# Revit family: AISC ST Shapes-Top
name_source: partatom
category: Detail Items
revit_build: Autodesk Revit Architecture 2012 (Build: 20110210_1515)
units: mm (PartAtom-declared; Revit-internal decimal feet)

## types (28) — shared parameters
Keynote = 05 12 00.J0
y = 0' - 2 15/16"

## per-type parameters (varying)
| type | A | W | bf | d | k | tf | tw |
| ST12X60.5 | 0.12 SF | 60.5 | 0' - 8 1/16" | 1' - 0 5/16" | 0' - 2" | 0' - 1 3/32" | 0' - 0 13/16" |
| ST12X53 | 0.11 SF | 53 | 0' - 7 7/8" | 1' - 0 5/16" | 0' - 2" | 0' - 1 3/32" | 0' - 0 5/8" |
| ST12X50 | 0.1 SF | 50 | 0' - 7 1/4" | 1' - 0" | 0' - 1 3/4" | 0' - 0 7/8" | 0' - 0 3/4" |
| ST12X45 | 0.09 SF | 45 | 0' - 7 1/8" | 1' - 0" | 0' - 1 3/4" | 0' - 0 7/8" | 0' - 0 5/8" |
| ST12X40 | 0.08 SF | 40 | 0' - 7" | 1' - 0" | 0' - 1 3/4" | 0' - 0 7/8" | 0' - 0 1/2" |
| ST10X48 | 0.1 SF | 48 | 0' - 7 3/16" | 0' - 10 3/16" | 0' - 1 3/4" | 0' - 0 29/32" | 0' - 0 13/16" |
| ST10X43 | 0.09 SF | 43 | 0' - 7 1/16" | 0' - 10 3/16" | 0' - 1 3/4" | 0' - 0 29/32" | 0' - 0 21/32" |
| ST10X37.5 | 0.08 SF | 37.5 | 0' - 6 3/8" | 0' - 10" | 0' - 1 5/8" | 0' - 0 25/32" | 0' - 0 5/8" |
| ST10X33 | 0.07 SF | 33 | 0' - 6 1/4" | 0' - 10" | 0' - 1 5/8" | 0' - 0 25/32" | 0' - 0 1/2" |
| ST9X35 | 0.07 SF | 35 | 0' - 6 1/4" | 0' - 9" | 0' - 1 1/2" | 0' - 0 11/16" | 0' - 0 23/32" |
| ST9X27.35 | 0.06 SF | 27.4 | 0' - 6" | 0' - 9" | 0' - 1 1/2" | 0' - 0 11/16" | 0' - 0 15/32" |
| ST7.5X25 | 0.05 SF | 25 | 0' - 5 5/8" | 0' - 7 1/2" | 0' - 1 3/8" | 0' - 0 5/8" | 0' - 0 9/16" |
| ST7.5X21.45 | 0.04 SF | 21.5 | 0' - 5 1/2" | 0' - 7 1/2" | 0' - 1 3/8" | 0' - 0 5/8" | 0' - 0 13/32" |
| ST6X25 | 0.05 SF | 25 | 0' - 5 15/32" | 0' - 6" | 0' - 1 7/16" | 0' - 0 21/32" | 0' - 0 11/16" |
| ST6X20.4 | 0.04 SF | 20.4 | 0' - 5 1/4" | 0' - 6" | 0' - 1 7/16" | 0' - 0 21/32" | 0' - 0 15/32" |
| ST6X17.5 | 0.04 SF | 17.5 | 0' - 5 3/32" | 0' - 6" | 0' - 1 3/16" | 0' - 0 17/32" | 0' - 0 7/16" |
| ST6X15.9 | 0.03 SF | 15.9 | 0' - 5" | 0' - 6" | 0' - 1 3/16" | 0' - 0 17/32" | 0' - 0 11/32" |
| ST5X17.5 | 0.04 SF | 17.5 | 0' - 4 15/16" | 0' - 5" | 0' - 1 1/8" | 0' - 0 1/2" | 0' - 0 19/32" |
| ST5X12.7 | 0.03 SF | 12.7 | 0' - 4 21/32" | 0' - 5" | 0' - 1 1/8" | 0' - 0 1/2" | 0' - 0 5/16" |
| ST4X11.5 | 0.02 SF | 11.5 | 0' - 4 5/32" | 0' - 4" | 0' - 1" | 0' - 0 7/16" | 0' - 0 7/16" |
| ST4X9.2 | 0.02 SF | 9.2 | 0' - 4" | 0' - 4" | 0' - 1" | 0' - 0 7/16" | 0' - 0 9/32" |
| ST3X8.6 | 0.02 SF | 8.6 | 0' - 3 9/16" | 0' - 3" | 0' - 0 13/16" | 0' - 0 11/32" | 0' - 0 15/32" |
| ST3X6.25 | 0.01 SF | 6.25 | 0' - 3 11/32" | 0' - 3" | 0' - 0 13/16" | 0' - 0 11/32" | 0' - 0 7/32" |
| ST2.5X5 | 0.01 SF | 5 | 0' - 3" | 0' - 2 1/2" | 0' - 0 3/4" | 0' - 0 5/16" | 0' - 0 7/32" |
| ST2X4.75 | 0.01 SF | 4.75 | 0' - 2 13/16" | 0' - 2" | 0' - 0 3/4" | 0' - 0 9/32" | 0' - 0 5/16" |
| ST2X3.85 | 0.01 SF | 3.85 | 0' - 2 21/32" | 0' - 2" | 0' - 0 3/4" | 0' - 0 9/32" | 0' - 0 3/16" |
| ST1.5X3.75 | 0.01 SF | 3.75 | 0' - 2 1/2" | 0' - 1 1/2" | 0' - 0 5/8" | 0' - 0 1/4" | 0' - 0 11/32" |
| ST1.5X2.85 | 0.01 SF | 2.85 | 0' - 2 11/32" | 0' - 1 1/2" | 0' - 0 5/8" | 0' - 0 1/4" | 0' - 0 5/32" |

## geometry (parser evidence)
native form markers: Sweep x1
no freeform markers — native parametric forms only
